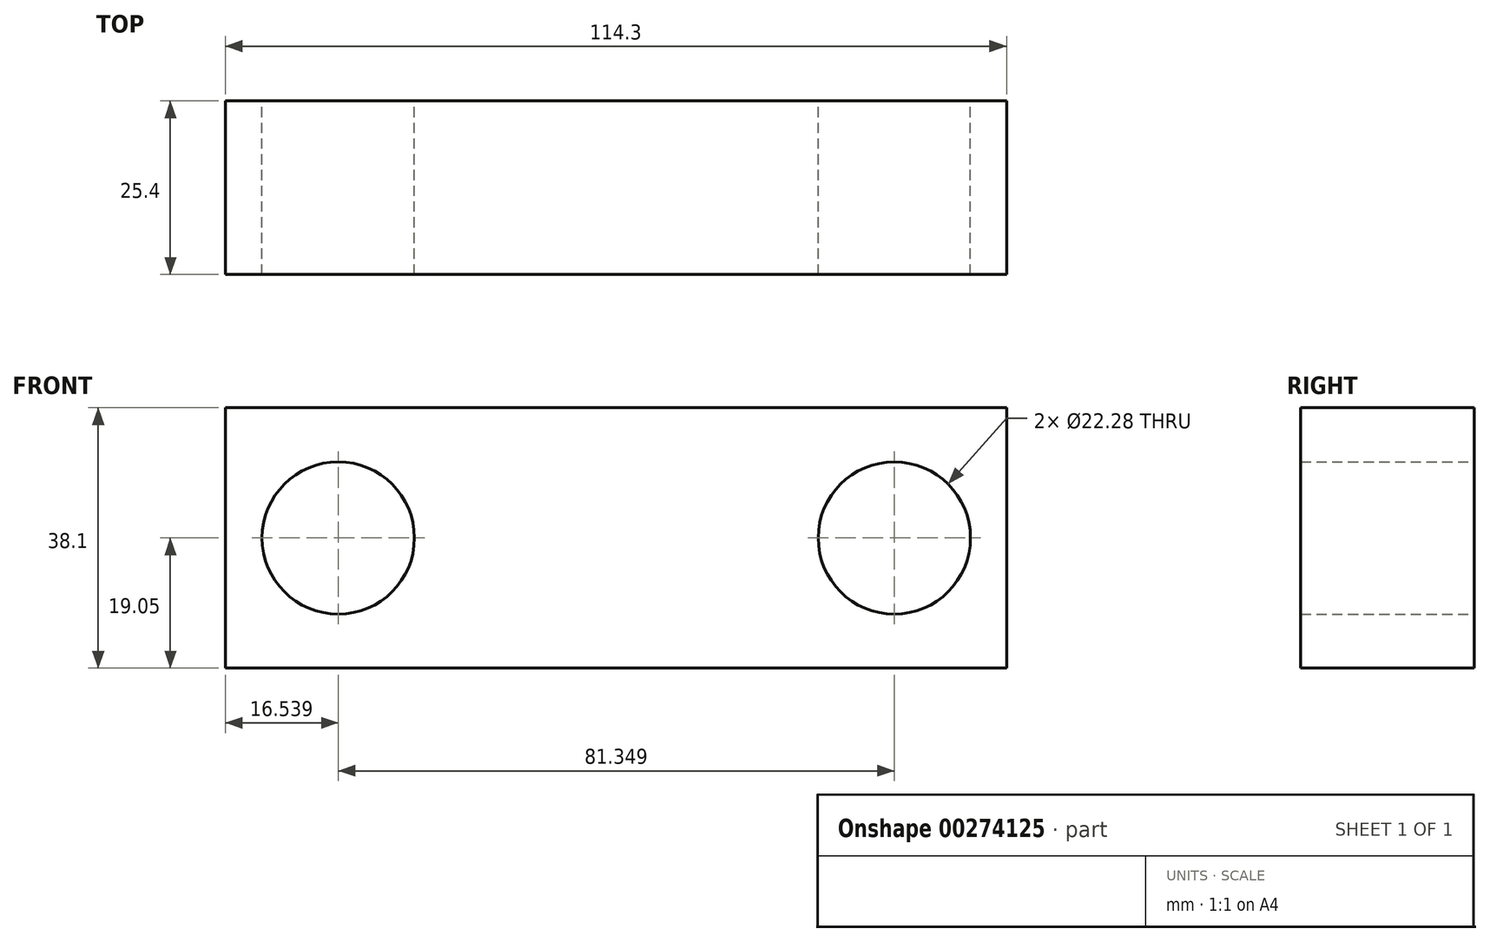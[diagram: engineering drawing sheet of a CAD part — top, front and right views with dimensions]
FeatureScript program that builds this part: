
annotation { "Feature Type Name" : "Feature", "Feature Type Description" : "" }
export const myFeature = defineFeature(function(context is Context, id is Id, definition is map)
    precondition{}
    {
        {
            var Q0;
            Q0=qCreatedBy(makeId("Front.planeOp"),FACE);
            var sketch = newSketch(context, id + "F0", { "sketchPlane" : qUnion([Q0])});
            skLineSegment(sketch, "E0.bottom", {"start": v(-57.15, -19.05) * mm, "end": v(57.15, -19.05) * mm});
            skLineSegment(sketch, "E0.top", {"start": v(-57.15, 19.05) * mm, "end": v(57.15, 19.05) * mm});
            skLineSegment(sketch, "E0.left", {"start": v(-57.15, -19.05) * mm, "end": v(-57.15, 19.05) * mm});
            skLineSegment(sketch, "E0.right", {"start": v(57.15, -19.05) * mm, "end": v(57.15, 19.05) * mm});
            skPoint(sketch, "E0.middle", {"position": v(0, 0) * mm});
            skSolve(sketch);
        }
        {
            var Q0;
            Q0=makeQuery(id+"F0.imprint","IMPRINT",FACE,{"disambiguationData":[TD([[makeQuery(id+"F0.imprint","IMPRINT",EDGE,{"derivedFrom":sQuery(id+"F0.wireOp",EDGE,"E0.bottom")}),1.0]])]});
            var sketch = newSketch(context, id + "F1", { "sketchPlane" : qUnion([Q0])});
            skCircle(sketch, "E1", {"center": v(-40.61, 0) * mm, "radius": 11.14 * mm});
            skCircle(sketch, "E2", {"center": v(40.74, 0) * mm, "radius": 11.14 * mm});
            skSolve(sketch);
        }
        {
            var Q0;
            Q0=makeQuery(id+"F0.imprint","IMPRINT",FACE,{"disambiguationData":[TD([[makeQuery(id+"F0.imprint","IMPRINT",EDGE,{"derivedFrom":sQuery(id+"F0.wireOp",EDGE,"E0.bottom")}),1.0]])]});
            var sketch = newSketch(context, id + "F2", { "sketchPlane" : qUnion([Q0])});
            skCircle(sketch, "E3", {"center": v(0, 0) * mm, "radius": 2.66 * mm});
            skSolve(sketch);
        }
        {
            var Q0;
            Q0=makeQuery(id+"F1.imprint","IMPRINT",FACE,{"disambiguationData":[TD([[makeQuery(id+"F1.imprint","IMPRINT",EDGE,{"derivedFrom":sQuery(id+"F1.wireOp",EDGE,"E1")}),-1.0]])]});
            extrude(context, id + "F3", {"entities" : qUnion([Q0]), "endBound" : BoundingType.SYMMETRIC, "depth" : 25.4 * mm});
        }
        {
            var Q0;
            Q0=sQuery(id+"F2.wireOp",EDGE,"E3");
            extrude(context, id + "F4", {"bodyType" : ToolBodyType.SURFACE, "surfaceEntities" : qUnion([Q0]), "endBound" : BoundingType.SYMMETRIC, "depth" : 25.4 * mm});
        }
    });
